# Revit family: Shower-Valve_Trim-KOHLER-ARTIFACTS-K-76966T_1
name_source: partatom
category: Specialty Equipment
revit_build: Autodesk Revit 2017 (Build: 20160225_1515(x64)
units: mm (PartAtom-declared; Revit-internal decimal feet)

## family parameters
Cut with Voids When Loaded = No
Host = Face
OmniClass Number = 23.31.25.00
OmniClass Title = Toilet and Bath Specialties
Part Type = Normal
Room Calculation Point = No
Round Connector Dimension = Use Diameter
Shared = No

## types (10) — shared parameters
ADA Compliant = No
Assembly Code = C1030200
Date Modified = 10/07/2020
Default Elevation = 42"
Description = Recessed Shower Bath Trim Kit With Divertor
Handle Clearance = 3 5/16"
Height = 7 1/16"
Length = 4 7/16"
Manufacturer = KOHLER Co.
Master Format 2014 = 10 28 00
Master Format 2014 Name = Toilet, Bath, and Laundry Accessories
Material = Premium Metal Construction
Product Name = ARTIFACTS
URL = http://www.kohler.com.cn
WaterSense Certified = No
Width = 7 1/16"

## per-type parameters (varying)
| type | Finish | Model | Type |
| CP-Polished Chrome | Kohler-Metal-CP-Polished_Chrome | K-76966T-4-CP | 1 |
| 2BL-Original Black | Kohler-Metal-2BL-Original_Black | K-76966T-4-2BL | 2 |
| 2BZ-Elegant Black | Kohler-Metal-2BZ-Oil_Rubbed_Bronze | K-76966T-4-2BZ | 3 |
| AF-Flange Gold | Kohler-Metal-AF-Vibrant_French_Gold | K-76966T-4-AF | 4 |
| BN-Roman Silver | Kohler-Metal-BN-Vibrant_Brushed_Nickel | K-76966T-4-BN | 5 |
| BV-Roman Copper | Kohler-Metal-BV-Brushed_Bronze | K-76966T-4-BV | 6 |
| PGD-Eternal Gold | Kohler-Metal-PGD-Modern_Polished_Gold | K-76966T-4-PGD | 7 |
| RGD- Rose Gold | Kohler-Metal-RGD-Polished_Rose_Gold | K-76966T-4-RGD | 8 |
| SN-Champagne Gold | Kohler-Metal-SN-Vibrant_Polished_Nickel | K-76966T-4-SN | 9 |
| TT-Titanium Silver | Kohler-Metal-TT-Vibrant_Titanium | K-76966T-4-TT | 10 |

## geometry (parser evidence)
native form markers: Sweep x5
no freeform markers — native parametric forms only
